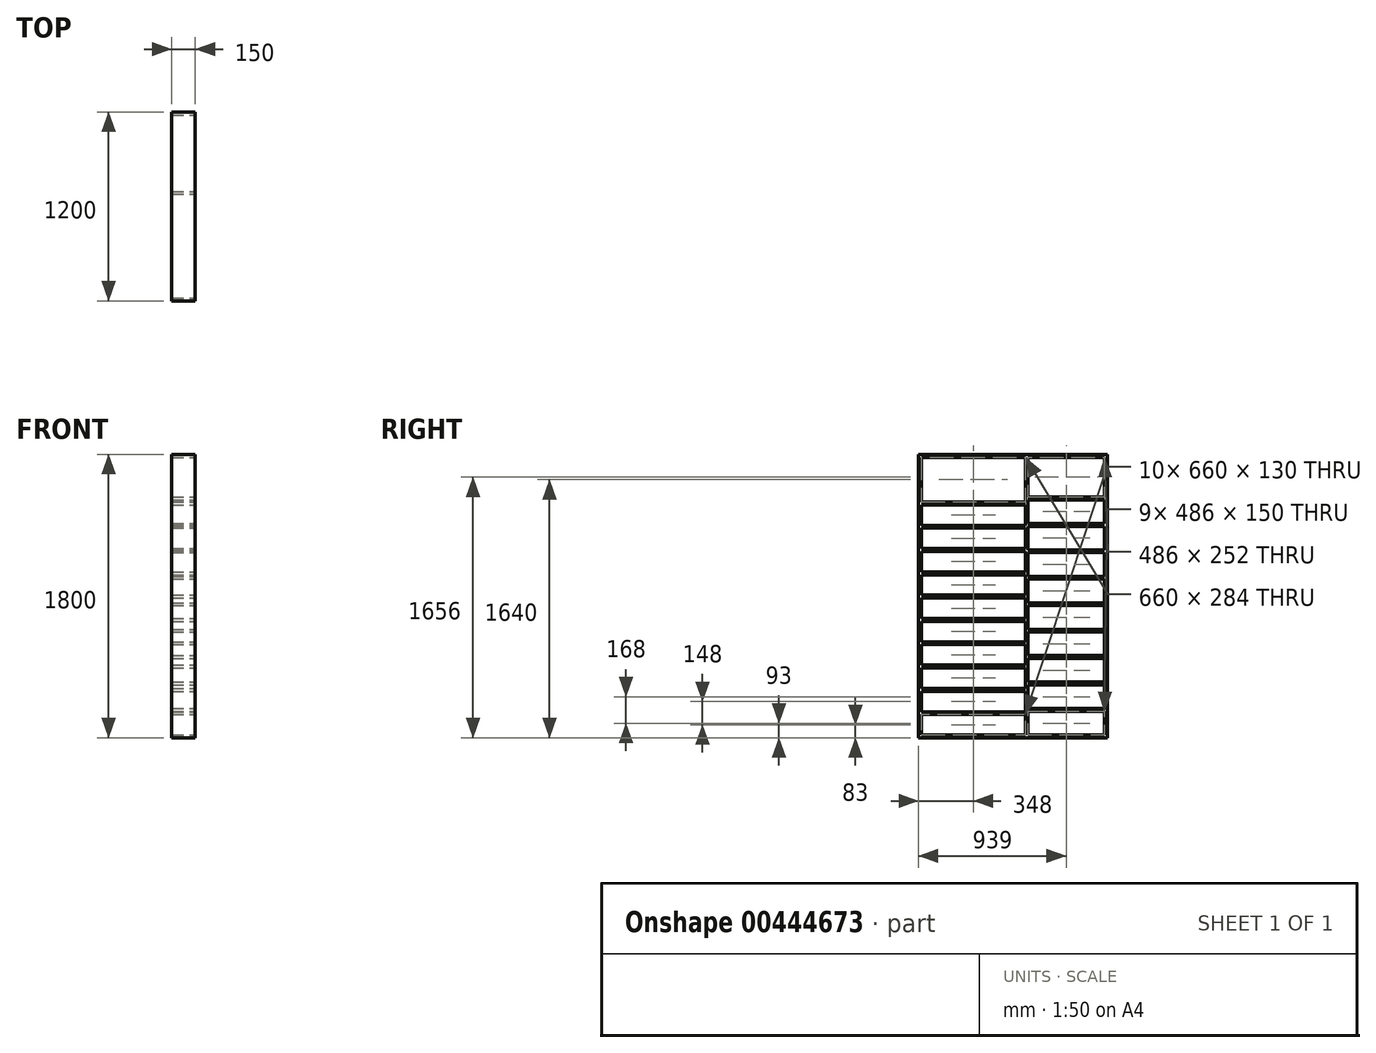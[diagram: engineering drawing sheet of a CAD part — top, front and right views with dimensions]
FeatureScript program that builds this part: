
annotation { "Feature Type Name" : "Feature", "Feature Type Description" : "" }
export const myFeature = defineFeature(function(context is Context, id is Id, definition is map)
    precondition{}
    {
        {
            var Q0;
            Q0=qCreatedBy(makeId("Right.planeOp"),FACE);
            var sketch = newSketch(context, id + "F0", { "sketchPlane" : qUnion([Q0])});
            skLineSegment(sketch, "E0.bottom", {"start": v(0, 0) * mm, "end": v(1200, 0) * mm});
            skLineSegment(sketch, "E0.top", {"start": v(0, 1800) * mm, "end": v(1200, 1800) * mm});
            skLineSegment(sketch, "E0.left", {"start": v(0, 0) * mm, "end": v(0, 1800) * mm});
            skLineSegment(sketch, "E0.right", {"start": v(1200, 0) * mm, "end": v(1200, 1800) * mm});
            skSolve(sketch);
        }
        {
            var Q0;
            Q0 = qSketchRegion(id + "F0", true);
            extrude(context, id + "F1", {"entities" : qUnion([Q0]), "depth" : 150 * mm});
        }
        {
            var Q0;
            Q0=makeQuery(id+"F1.opExtrude","CAP_FACE",FACE,{"disambiguationData":[OSD([sQuery(id+"F0.wireOp",EDGE,"E0.bottom"),sQuery(id+"F0.wireOp",EDGE,"E0.top"),sQuery(id+"F0.wireOp",EDGE,"E0.left"),sQuery(id+"F0.wireOp",EDGE,"E0.right")])],"isStart":false});
            var sketch = newSketch(context, id + "F2", { "sketchPlane" : qUnion([Q0])});
            skLineSegment(sketch, "E1.bottom", {"start": v(18, 1782) * mm, "end": v(1182, 1782) * mm});
            skLineSegment(sketch, "E1.top", {"start": v(18, 18) * mm, "end": v(1182, 18) * mm});
            skLineSegment(sketch, "E1.left", {"start": v(18, 1782) * mm, "end": v(18, 18) * mm});
            skLineSegment(sketch, "E1.right", {"start": v(1182, 1782) * mm, "end": v(1182, 18) * mm});
            skLineSegment(sketch, "E2.0", {"start": v(0, 0) * mm, "end": v(0, 1800) * mm});
            skLineSegment(sketch, "E3.0", {"start": v(0, 1800) * mm, "end": v(1200, 1800) * mm});
            skLineSegment(sketch, "E4.0", {"start": v(1200, 0) * mm, "end": v(1200, 1800) * mm});
            skLineSegment(sketch, "E5.0", {"start": v(0, 0) * mm, "end": v(1200, 0) * mm});
            skSolve(sketch);
        }
        {
            var Q0;
            Q0=makeQuery(id+"F2.imprint","IMPRINT",FACE,{"disambiguationData":[TD([[makeQuery(id+"F2.imprint","IMPRINT",EDGE,{"derivedFrom":sQuery(id+"F2.wireOp",EDGE,"E1.bottom")}),-1.0]])]});
            extrude(context, id + "F3", {"entities" : qUnion([Q0]), "operationType" : NewBodyOperationType.REMOVE, "oppositeDirection" : true, "depth" : 150 * mm});
        }
        {
            var Q0;
            Q0=makeQuery(id+"F3.boolean.opBoolean","COPY",FACE,{"derivedFrom":makeQuery(id+"F3.opExtrude","SWEPT_FACE",FACE,{"disambiguationData":[OSD([sQuery(id+"F2.wireOp",EDGE,"E1.top")])]})});
            var sketch = newSketch(context, id + "F4", { "sketchPlane" : qUnion([Q0])});
            skLineSegment(sketch, "E6.bottom", {"start": v(0, 678) * mm, "end": v(150, 678) * mm});
            skLineSegment(sketch, "E6.top", {"start": v(0, 696) * mm, "end": v(150, 696) * mm});
            skLineSegment(sketch, "E6.left", {"start": v(0, 678) * mm, "end": v(0, 696) * mm});
            skLineSegment(sketch, "E6.right", {"start": v(150, 678) * mm, "end": v(150, 696) * mm});
            skSolve(sketch);
        }
        {
            var Q0;
            Q0 = qSketchRegion(id + "F4", true);
            extrude(context, id + "F5", {"entities" : qUnion([Q0]), "operationType" : NewBodyOperationType.ADD, "depth" : 1764 * mm});
        }
        {
            var Q0;
            Q0=makeQuery(id+"F5.opExtrude","SWEPT_FACE",FACE,{"disambiguationData":[OSD([sQuery(id+"F4.wireOp",EDGE,"E6.bottom")])]});
            var sketch = newSketch(context, id + "F6", { "sketchPlane" : qUnion([Q0])});
            skLineSegment(sketch, "E7.bottom", {"start": v(0, 166) * mm, "end": v(150, 166) * mm});
            skLineSegment(sketch, "E7.top", {"start": v(0, 148) * mm, "end": v(150, 148) * mm});
            skLineSegment(sketch, "E7.left", {"start": v(0, 166) * mm, "end": v(0, 148) * mm});
            skLineSegment(sketch, "E7.right", {"start": v(150, 166) * mm, "end": v(150, 148) * mm});
            skLineSegment(sketch, "E8.0.1.0", {"start": v(0, 314) * mm, "end": v(0, 296) * mm});
            skLineSegment(sketch, "E8.0.1.1", {"start": v(0, 314) * mm, "end": v(150, 314) * mm});
            skLineSegment(sketch, "E8.0.1.2", {"start": v(150, 314) * mm, "end": v(150, 296) * mm});
            skLineSegment(sketch, "E8.0.1.3", {"start": v(0, 296) * mm, "end": v(150, 296) * mm});
            skLineSegment(sketch, "E8.0.2.0", {"start": v(0, 462) * mm, "end": v(0, 444) * mm});
            skLineSegment(sketch, "E8.0.2.1", {"start": v(0, 462) * mm, "end": v(150, 462) * mm});
            skLineSegment(sketch, "E8.0.2.2", {"start": v(150, 462) * mm, "end": v(150, 444) * mm});
            skLineSegment(sketch, "E8.0.2.3", {"start": v(0, 444) * mm, "end": v(150, 444) * mm});
            skLineSegment(sketch, "E8.0.3.0", {"start": v(0, 610) * mm, "end": v(0, 592) * mm});
            skLineSegment(sketch, "E8.0.3.1", {"start": v(0, 610) * mm, "end": v(150, 610) * mm});
            skLineSegment(sketch, "E8.0.3.2", {"start": v(150, 610) * mm, "end": v(150, 592) * mm});
            skLineSegment(sketch, "E8.0.3.3", {"start": v(0, 592) * mm, "end": v(150, 592) * mm});
            skLineSegment(sketch, "E8.0.4.0", {"start": v(0, 758) * mm, "end": v(0, 740) * mm});
            skLineSegment(sketch, "E8.0.4.1", {"start": v(0, 758) * mm, "end": v(150, 758) * mm});
            skLineSegment(sketch, "E8.0.4.2", {"start": v(150, 758) * mm, "end": v(150, 740) * mm});
            skLineSegment(sketch, "E8.0.4.3", {"start": v(0, 740) * mm, "end": v(150, 740) * mm});
            skLineSegment(sketch, "E8.0.5.0", {"start": v(0, 906) * mm, "end": v(0, 888) * mm});
            skLineSegment(sketch, "E8.0.5.1", {"start": v(0, 906) * mm, "end": v(150, 906) * mm});
            skLineSegment(sketch, "E8.0.5.2", {"start": v(150, 906) * mm, "end": v(150, 888) * mm});
            skLineSegment(sketch, "E8.0.5.3", {"start": v(0, 888) * mm, "end": v(150, 888) * mm});
            skLineSegment(sketch, "E8.0.6.0", {"start": v(0, 1054) * mm, "end": v(0, 1036) * mm});
            skLineSegment(sketch, "E8.0.6.1", {"start": v(0, 1054) * mm, "end": v(150, 1054) * mm});
            skLineSegment(sketch, "E8.0.6.2", {"start": v(150, 1054) * mm, "end": v(150, 1036) * mm});
            skLineSegment(sketch, "E8.0.6.3", {"start": v(0, 1036) * mm, "end": v(150, 1036) * mm});
            skLineSegment(sketch, "E8.0.7.0", {"start": v(0, 1202) * mm, "end": v(0, 1184) * mm});
            skLineSegment(sketch, "E8.0.7.1", {"start": v(0, 1202) * mm, "end": v(150, 1202) * mm});
            skLineSegment(sketch, "E8.0.7.2", {"start": v(150, 1202) * mm, "end": v(150, 1184) * mm});
            skLineSegment(sketch, "E8.0.7.3", {"start": v(0, 1184) * mm, "end": v(150, 1184) * mm});
            skLineSegment(sketch, "E8.0.8.0", {"start": v(0, 1350) * mm, "end": v(0, 1332) * mm});
            skLineSegment(sketch, "E8.0.8.1", {"start": v(0, 1350) * mm, "end": v(150, 1350) * mm});
            skLineSegment(sketch, "E8.0.8.2", {"start": v(150, 1350) * mm, "end": v(150, 1332) * mm});
            skLineSegment(sketch, "E8.0.8.3", {"start": v(0, 1332) * mm, "end": v(150, 1332) * mm});
            skLineSegment(sketch, "E8.0.9.0", {"start": v(0, 1498) * mm, "end": v(0, 1480) * mm});
            skLineSegment(sketch, "E8.0.9.1", {"start": v(0, 1498) * mm, "end": v(150, 1498) * mm});
            skLineSegment(sketch, "E8.0.9.2", {"start": v(150, 1498) * mm, "end": v(150, 1480) * mm});
            skLineSegment(sketch, "E8.0.9.3", {"start": v(0, 1480) * mm, "end": v(150, 1480) * mm});
            skLineSegment(sketch, "E8.direction1", {"start": v(0, 148) * mm, "end": v(25, 148) * mm, "construction": true});
            skLineSegment(sketch, "E8.direction2", {"start": v(0, 148) * mm, "end": v(0, 296) * mm, "construction": true});
            skSolve(sketch);
        }
        {
            var Q0;
            Q0=makeQuery(id+"F6.imprint","IMPRINT",FACE,{"disambiguationData":[TD([[makeQuery(id+"F6.imprint","IMPRINT",EDGE,{"derivedFrom":sQuery(id+"F6.wireOp",EDGE,"E7.bottom")}),-1.0]])]});
            var Q1;
            Q1=makeQuery(id+"F6.imprint","IMPRINT",FACE,{"disambiguationData":[TD([[makeQuery(id+"F6.imprint","IMPRINT",EDGE,{"derivedFrom":sQuery(id+"F6.wireOp",EDGE,"E8.0.1.0")}),1.0]])]});
            var Q2;
            Q2=makeQuery(id+"F6.imprint","IMPRINT",FACE,{"disambiguationData":[TD([[makeQuery(id+"F6.imprint","IMPRINT",EDGE,{"derivedFrom":sQuery(id+"F6.wireOp",EDGE,"E8.0.2.0")}),1.0]])]});
            var Q3;
            Q3=makeQuery(id+"F6.imprint","IMPRINT",FACE,{"disambiguationData":[TD([[makeQuery(id+"F6.imprint","IMPRINT",EDGE,{"derivedFrom":sQuery(id+"F6.wireOp",EDGE,"E8.0.3.0")}),1.0]])]});
            var Q4;
            Q4=makeQuery(id+"F6.imprint","IMPRINT",FACE,{"disambiguationData":[TD([[makeQuery(id+"F6.imprint","IMPRINT",EDGE,{"derivedFrom":sQuery(id+"F6.wireOp",EDGE,"E8.0.4.0")}),1.0]])]});
            var Q5;
            Q5=makeQuery(id+"F6.imprint","IMPRINT",FACE,{"disambiguationData":[TD([[makeQuery(id+"F6.imprint","IMPRINT",EDGE,{"derivedFrom":sQuery(id+"F6.wireOp",EDGE,"E8.0.5.0")}),1.0]])]});
            var Q6;
            Q6=makeQuery(id+"F6.imprint","IMPRINT",FACE,{"disambiguationData":[TD([[makeQuery(id+"F6.imprint","IMPRINT",EDGE,{"derivedFrom":sQuery(id+"F6.wireOp",EDGE,"E8.0.6.0")}),1.0]])]});
            var Q7;
            Q7=makeQuery(id+"F6.imprint","IMPRINT",FACE,{"disambiguationData":[TD([[makeQuery(id+"F6.imprint","IMPRINT",EDGE,{"derivedFrom":sQuery(id+"F6.wireOp",EDGE,"E8.0.7.0")}),1.0]])]});
            var Q8;
            Q8=makeQuery(id+"F6.imprint","IMPRINT",FACE,{"disambiguationData":[TD([[makeQuery(id+"F6.imprint","IMPRINT",EDGE,{"derivedFrom":sQuery(id+"F6.wireOp",EDGE,"E8.0.8.0")}),1.0]])]});
            var Q9;
            Q9=makeQuery(id+"F6.imprint","IMPRINT",FACE,{"disambiguationData":[TD([[makeQuery(id+"F6.imprint","IMPRINT",EDGE,{"derivedFrom":sQuery(id+"F6.wireOp",EDGE,"E8.0.9.0")}),1.0]])]});
            extrude(context, id + "F7", {"entities" : qUnion([Q0, Q1, Q2, Q3, Q4, Q5, Q6, Q7, Q8, Q9]), "operationType" : NewBodyOperationType.ADD, "depth" : 660 * mm});
        }
        {
            var Q0;
            Q0=makeQuery(id+"F3.boolean.opBoolean","COPY",FACE,{"derivedFrom":makeQuery(id+"F3.opExtrude","SWEPT_FACE",FACE,{"disambiguationData":[OSD([sQuery(id+"F2.wireOp",EDGE,"E1.right")])]})});
            var sketch = newSketch(context, id + "F8", { "sketchPlane" : qUnion([Q0])});
            skLineSegment(sketch, "E9.bottom", {"start": v(0, 186) * mm, "end": v(150, 186) * mm});
            skLineSegment(sketch, "E9.top", {"start": v(0, 168) * mm, "end": v(150, 168) * mm});
            skLineSegment(sketch, "E9.left", {"start": v(0, 186) * mm, "end": v(0, 168) * mm});
            skLineSegment(sketch, "E9.right", {"start": v(150, 186) * mm, "end": v(150, 168) * mm});
            skLineSegment(sketch, "E10.0.1.0", {"start": v(0, 354) * mm, "end": v(0, 336) * mm});
            skLineSegment(sketch, "E10.0.1.1", {"start": v(0, 354) * mm, "end": v(150, 354) * mm});
            skLineSegment(sketch, "E10.0.1.2", {"start": v(0, 336) * mm, "end": v(150, 336) * mm});
            skLineSegment(sketch, "E10.0.1.3", {"start": v(150, 354) * mm, "end": v(150, 336) * mm});
            skLineSegment(sketch, "E10.0.2.0", {"start": v(0, 522) * mm, "end": v(0, 504) * mm});
            skLineSegment(sketch, "E10.0.2.1", {"start": v(0, 522) * mm, "end": v(150, 522) * mm});
            skLineSegment(sketch, "E10.0.2.2", {"start": v(0, 504) * mm, "end": v(150, 504) * mm});
            skLineSegment(sketch, "E10.0.2.3", {"start": v(150, 522) * mm, "end": v(150, 504) * mm});
            skLineSegment(sketch, "E10.0.3.0", {"start": v(0, 690) * mm, "end": v(0, 672) * mm});
            skLineSegment(sketch, "E10.0.3.1", {"start": v(0, 690) * mm, "end": v(150, 690) * mm});
            skLineSegment(sketch, "E10.0.3.2", {"start": v(0, 672) * mm, "end": v(150, 672) * mm});
            skLineSegment(sketch, "E10.0.3.3", {"start": v(150, 690) * mm, "end": v(150, 672) * mm});
            skLineSegment(sketch, "E10.0.4.0", {"start": v(0, 858) * mm, "end": v(0, 840) * mm});
            skLineSegment(sketch, "E10.0.4.1", {"start": v(0, 858) * mm, "end": v(150, 858) * mm});
            skLineSegment(sketch, "E10.0.4.2", {"start": v(0, 840) * mm, "end": v(150, 840) * mm});
            skLineSegment(sketch, "E10.0.4.3", {"start": v(150, 858) * mm, "end": v(150, 840) * mm});
            skLineSegment(sketch, "E10.0.5.0", {"start": v(0, 1026) * mm, "end": v(0, 1008) * mm});
            skLineSegment(sketch, "E10.0.5.1", {"start": v(0, 1026) * mm, "end": v(150, 1026) * mm});
            skLineSegment(sketch, "E10.0.5.2", {"start": v(0, 1008) * mm, "end": v(150, 1008) * mm});
            skLineSegment(sketch, "E10.0.5.3", {"start": v(150, 1026) * mm, "end": v(150, 1008) * mm});
            skLineSegment(sketch, "E10.0.6.0", {"start": v(0, 1194) * mm, "end": v(0, 1176) * mm});
            skLineSegment(sketch, "E10.0.6.1", {"start": v(0, 1194) * mm, "end": v(150, 1194) * mm});
            skLineSegment(sketch, "E10.0.6.2", {"start": v(0, 1176) * mm, "end": v(150, 1176) * mm});
            skLineSegment(sketch, "E10.0.6.3", {"start": v(150, 1194) * mm, "end": v(150, 1176) * mm});
            skLineSegment(sketch, "E10.0.7.0", {"start": v(0, 1362) * mm, "end": v(0, 1344) * mm});
            skLineSegment(sketch, "E10.0.7.1", {"start": v(0, 1362) * mm, "end": v(150, 1362) * mm});
            skLineSegment(sketch, "E10.0.7.2", {"start": v(0, 1344) * mm, "end": v(150, 1344) * mm});
            skLineSegment(sketch, "E10.0.7.3", {"start": v(150, 1362) * mm, "end": v(150, 1344) * mm});
            skLineSegment(sketch, "E10.0.8.0", {"start": v(0, 1530) * mm, "end": v(0, 1512) * mm});
            skLineSegment(sketch, "E10.0.8.1", {"start": v(0, 1530) * mm, "end": v(150, 1530) * mm});
            skLineSegment(sketch, "E10.0.8.2", {"start": v(0, 1512) * mm, "end": v(150, 1512) * mm});
            skLineSegment(sketch, "E10.0.8.3", {"start": v(150, 1530) * mm, "end": v(150, 1512) * mm});
            skLineSegment(sketch, "E10.direction1", {"start": v(0, 168) * mm, "end": v(25, 168) * mm, "construction": true});
            skLineSegment(sketch, "E10.direction2", {"start": v(0, 168) * mm, "end": v(0, 336) * mm, "construction": true});
            skSolve(sketch);
        }
        {
            var Q0;
            Q0=makeQuery(id+"F8.imprint","IMPRINT",FACE,{"disambiguationData":[TD([[makeQuery(id+"F8.imprint","IMPRINT",EDGE,{"derivedFrom":sQuery(id+"F8.wireOp",EDGE,"E9.bottom")}),-1.0]])]});
            var Q1;
            Q1=makeQuery(id+"F8.imprint","IMPRINT",FACE,{"disambiguationData":[TD([[makeQuery(id+"F8.imprint","IMPRINT",EDGE,{"derivedFrom":sQuery(id+"F8.wireOp",EDGE,"E10.0.1.0")}),1.0]])]});
            var Q2;
            Q2=makeQuery(id+"F8.imprint","IMPRINT",FACE,{"disambiguationData":[TD([[makeQuery(id+"F8.imprint","IMPRINT",EDGE,{"derivedFrom":sQuery(id+"F8.wireOp",EDGE,"E10.0.2.0")}),1.0]])]});
            var Q3;
            Q3=makeQuery(id+"F8.imprint","IMPRINT",FACE,{"disambiguationData":[TD([[makeQuery(id+"F8.imprint","IMPRINT",EDGE,{"derivedFrom":sQuery(id+"F8.wireOp",EDGE,"E10.0.3.0")}),1.0]])]});
            var Q4;
            Q4=makeQuery(id+"F8.imprint","IMPRINT",FACE,{"disambiguationData":[TD([[makeQuery(id+"F8.imprint","IMPRINT",EDGE,{"derivedFrom":sQuery(id+"F8.wireOp",EDGE,"E10.0.4.0")}),1.0]])]});
            var Q5;
            Q5=makeQuery(id+"F8.imprint","IMPRINT",FACE,{"disambiguationData":[TD([[makeQuery(id+"F8.imprint","IMPRINT",EDGE,{"derivedFrom":sQuery(id+"F8.wireOp",EDGE,"E10.0.5.0")}),1.0]])]});
            var Q6;
            Q6=makeQuery(id+"F8.imprint","IMPRINT",FACE,{"disambiguationData":[TD([[makeQuery(id+"F8.imprint","IMPRINT",EDGE,{"derivedFrom":sQuery(id+"F8.wireOp",EDGE,"E10.0.6.0")}),1.0]])]});
            var Q7;
            Q7=makeQuery(id+"F8.imprint","IMPRINT",FACE,{"disambiguationData":[TD([[makeQuery(id+"F8.imprint","IMPRINT",EDGE,{"derivedFrom":sQuery(id+"F8.wireOp",EDGE,"E10.0.7.0")}),1.0]])]});
            var Q8;
            Q8=makeQuery(id+"F8.imprint","IMPRINT",FACE,{"disambiguationData":[TD([[makeQuery(id+"F8.imprint","IMPRINT",EDGE,{"derivedFrom":sQuery(id+"F8.wireOp",EDGE,"E10.0.8.0")}),1.0]])]});
            extrude(context, id + "F9", {"entities" : qUnion([Q0, Q1, Q2, Q3, Q4, Q5, Q6, Q7, Q8]), "operationType" : NewBodyOperationType.ADD, "depth" : 486 * mm});
        }
    });
